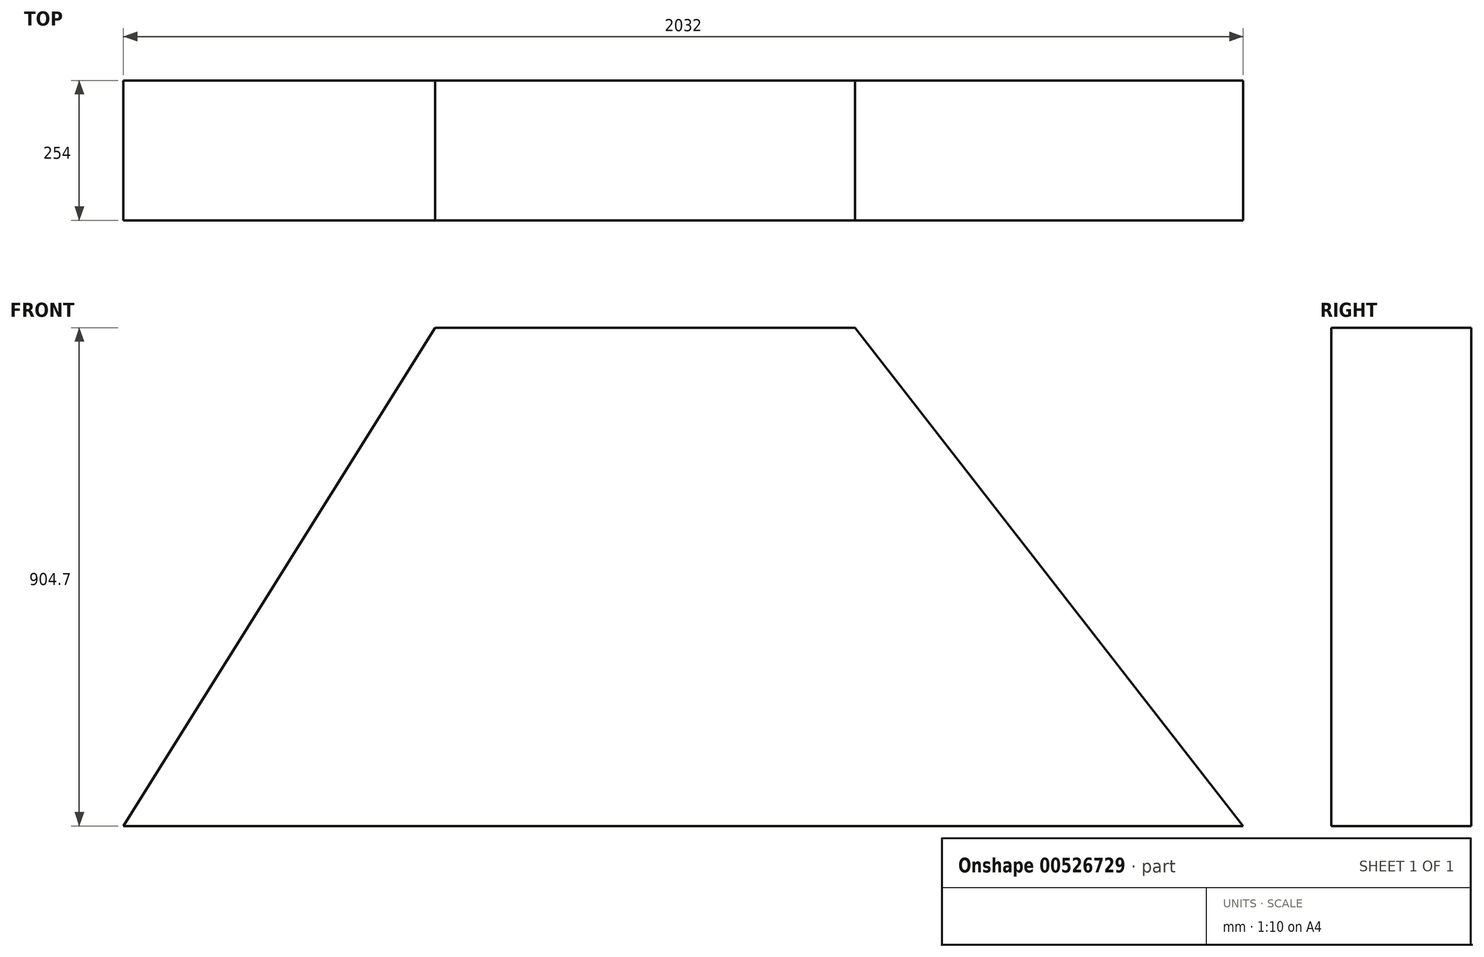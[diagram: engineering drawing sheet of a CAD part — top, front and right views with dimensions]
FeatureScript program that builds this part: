
annotation { "Feature Type Name" : "Feature", "Feature Type Description" : "" }
export const myFeature = defineFeature(function(context is Context, id is Id, definition is map)
    precondition{}
    {
        {
            var Q0;
            Q0=qCreatedBy(makeId("Front.planeOp"),FACE);
            var sketch = newSketch(context, id + "F0", { "sketchPlane" : qUnion([Q0])});
            skLineSegment(sketch, "E0", {"start": v(0, 0) * mm, "end": v(-2032, 0) * mm});
            skLineSegment(sketch, "E1", {"start": v(-2032, 0) * mm, "end": v(-1466.68, 904.7) * mm});
            skLineSegment(sketch, "E2", {"start": v(-1466.68, 904.7) * mm, "end": v(-704.68, 904.7) * mm});
            skLineSegment(sketch, "E3", {"start": v(-704.68, 904.7) * mm, "end": v(0, 0) * mm});
            skSolve(sketch);
        }
        {
            var Q0;
            Q0 = qSketchRegion(id + "F0", true);
            extrude(context, id + "F1", {"entities" : qUnion([Q0]), "depth" : 254 * mm, "offsetDistance" : 25.4 * mm});
        }
    });
